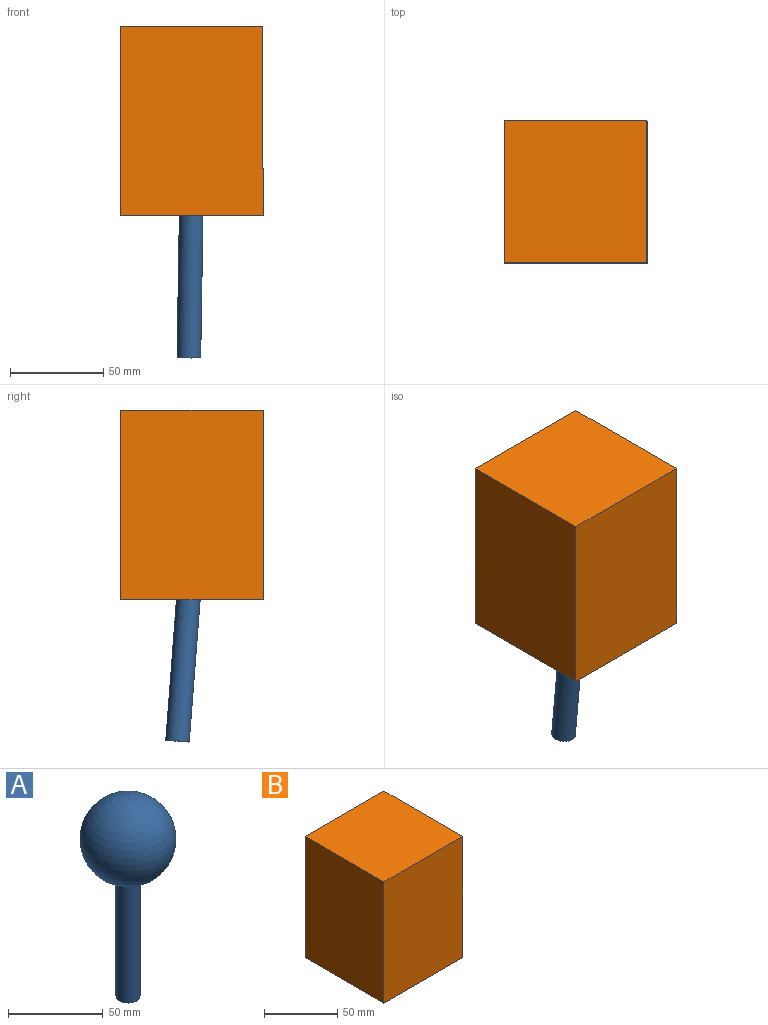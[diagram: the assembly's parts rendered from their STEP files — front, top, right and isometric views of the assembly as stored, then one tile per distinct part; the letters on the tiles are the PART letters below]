
ASSEMBLY  parts=2 mates=1
PART A: 3 faces, bbox 50.8x50.8x127 mm
  f0: sphere r=25.4mm, area 7978.6mm2, adj f1
  f1: cylinder r=6.35mm len=77.01mm, axis (0,0,1), area 3072.4mm2, adj f0,f2
  f2: plane 12.7x12.7mm, normal (0,0,-1), area 126.7mm2, adj f1
PART B: 14 faces, bbox 76.3x76.2x101.6 mm
  f0: plane 50.8x50.8mm, normal (0,0,1), area 1520.1mm2, adj f2,f3
  f1: plane 50.8x50.8mm, normal (0,0,-1), area 2026.8mm2, adj f2
  f2: cylinder r=25.4mm len=50.82mm, axis (0,0,1), area 8110.1mm2, adj f0,f1
  f3: cylinder r=12.7mm len=25.4mm, axis (0,0,1), area 2026.8mm2, adj f0,f11
  f4: plane 76.22x76.2mm, normal (1,0,0), area 5807.8mm2, adj f5,f7,f8,f13
  f5: plane 101.62x76.3mm, normal (0,1,0), area 7745.9mm2, adj f4,f6,f8,f9,f10,f11,f12,f13
  f6: plane 101.6x76.2mm, normal (-1,0,0), area 7741.9mm2, adj f5,f7,f8,f9
  f7: plane 101.62x76.3mm, normal (0,-1,0), area 7745.9mm2, adj f4,f6,f8,f9,f10,f11,f12,f13
  f8: plane 76.2x76.2mm, normal (0,0,1), area 5806.4mm2, adj f4,f5,f6,f7
  f9: plane 76.2x0.1mm, normal (0,0,-1), area 7.9mm2, adj f5,f6,f7,f10
  f10: plane 76.2x0.02mm, normal (-1,0,0), area 1.3mm2, adj f5,f7,f9,f11
  f11: plane 76.2x76.2mm, normal (0,0,-1), area 5299.7mm2, adj f3,f5,f7,f10,f12
  f12: plane 76.2x25.4mm, normal (1,0,0), area 1935.5mm2, adj f5,f7,f11,f13
  f13: plane 76.2x0.1mm, normal (0,0,1), area 7.9mm2, adj f4,f5,f7,f12
PLACE A rot(axis=(-0.01,0.04,-1),175.6deg) t=(-8.87,5.79,-9.06)mm
PLACE B t=(-8.87,5.79,16.36)mm fixed
MATE ball B.f2 <-> A.f1  axis (0,0,1) through (-8.87,5.79,-9.06)mm
